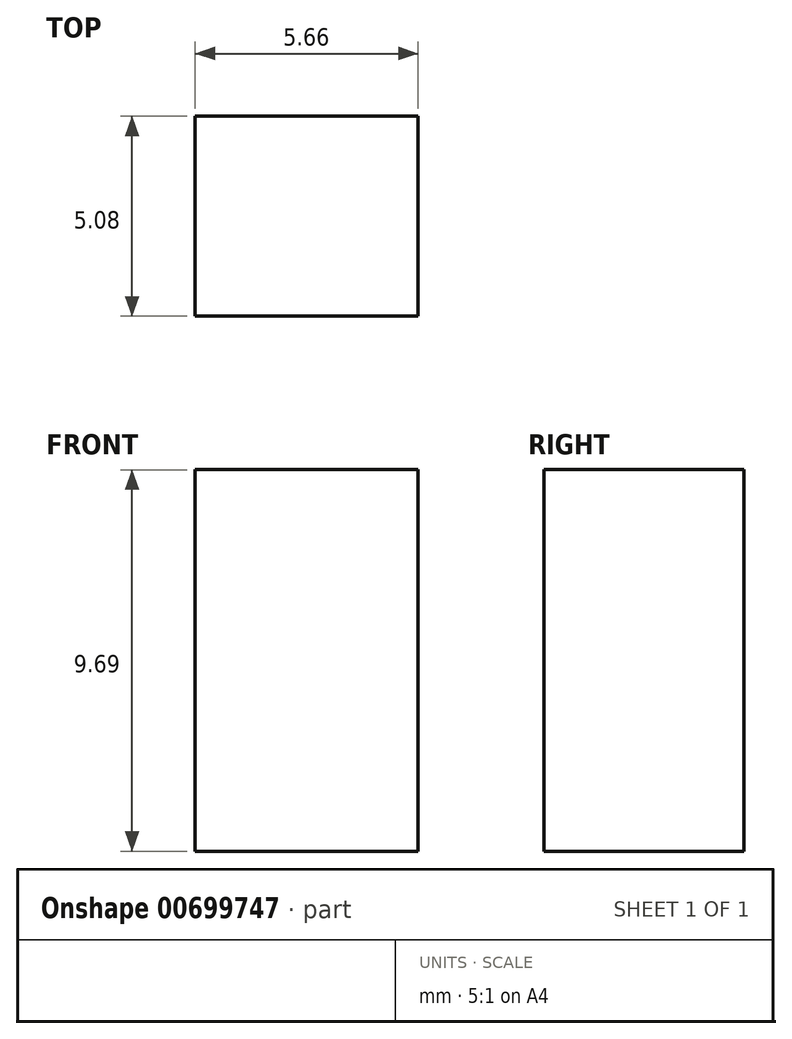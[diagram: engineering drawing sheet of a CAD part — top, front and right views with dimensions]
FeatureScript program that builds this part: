
annotation { "Feature Type Name" : "Feature", "Feature Type Description" : "" }
export const myFeature = defineFeature(function(context is Context, id is Id, definition is map)
    precondition{}
    {
        {
            var Q0;
            Q0=qCreatedBy(makeId("Front.planeOp"),FACE);
            var sketch = newSketch(context, id + "F0", { "sketchPlane" : qUnion([Q0])});
            skLineSegment(sketch, "E0.bottom", {"start": v(-127.41, 39.15) * mm, "end": v(-121.75, 39.15) * mm});
            skLineSegment(sketch, "E0.top", {"start": v(-127.41, 29.46) * mm, "end": v(-121.75, 29.46) * mm});
            skLineSegment(sketch, "E0.left", {"start": v(-127.41, 39.15) * mm, "end": v(-127.41, 29.46) * mm});
            skLineSegment(sketch, "E0.right", {"start": v(-121.75, 39.15) * mm, "end": v(-121.75, 29.46) * mm});
            skSolve(sketch);
        }
        {
            var Q0;
            Q0 = qSketchRegion(id + "F0", true);
            extrude(context, id + "F1", {"entities" : qUnion([Q0]), "depth" : 5.08 * mm, "offsetDistance" : 25.4 * mm});
        }
    });
